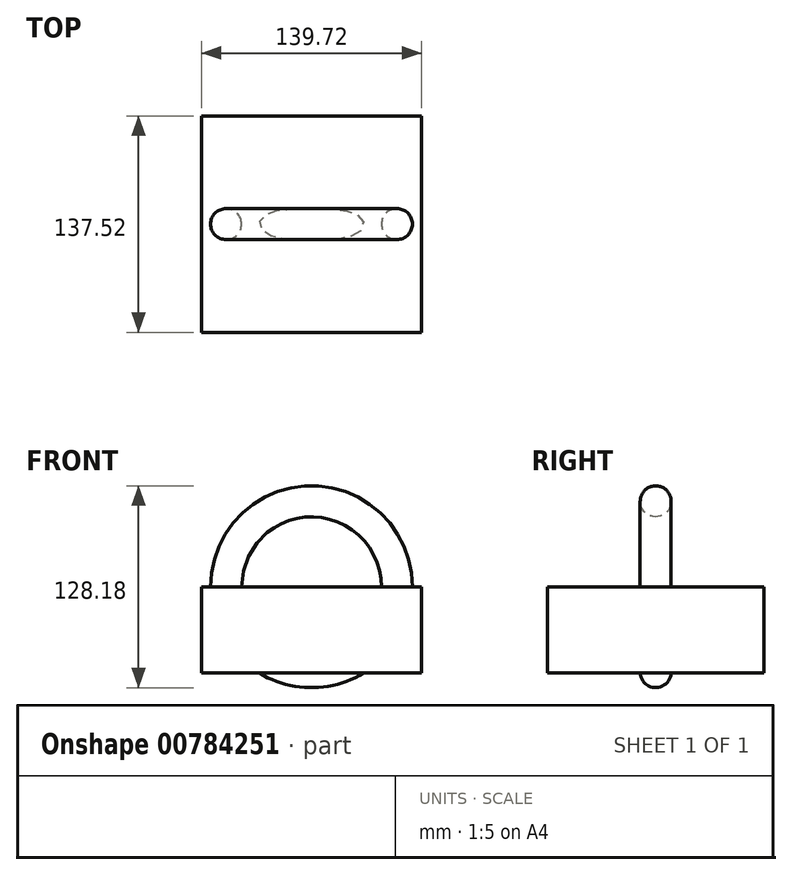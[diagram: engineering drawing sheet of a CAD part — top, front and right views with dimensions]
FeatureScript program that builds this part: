
annotation { "Feature Type Name" : "Feature", "Feature Type Description" : "" }
export const myFeature = defineFeature(function(context is Context, id is Id, definition is map)
    precondition{}
    {
        {
            var Q0;
            Q0=qCreatedBy(makeId("Top.planeOp"),FACE);
            var sketch = newSketch(context, id + "F0", { "sketchPlane" : qUnion([Q0])});
            skLineSegment(sketch, "E0.bottom", {"start": v(69.86, -68.76) * mm, "end": v(-69.86, -68.76) * mm});
            skLineSegment(sketch, "E0.top", {"start": v(69.86, 68.76) * mm, "end": v(-69.86, 68.76) * mm});
            skLineSegment(sketch, "E0.left", {"start": v(69.86, -68.76) * mm, "end": v(69.86, 68.76) * mm});
            skLineSegment(sketch, "E0.right", {"start": v(-69.86, -68.76) * mm, "end": v(-69.86, 68.76) * mm});
            skPoint(sketch, "E0.middle", {"position": v(0, 0) * mm});
            skLineSegment(sketch, "E1", {"start": v(0, 68.76) * mm, "end": v(0, -68.76) * mm});
            skSolve(sketch);
        }
        {
            var Q0;
            Q0=qCreatedBy(makeId("Top.planeOp"),FACE);
            var sketch = newSketch(context, id + "F1", { "sketchPlane" : qUnion([Q0])});
            skCircle(sketch, "E2", {"center": v(54.26, 0) * mm, "radius": 9.82 * mm});
            skSolve(sketch);
        }
        {
            var Q0;
            {var subQ0=sQuery(id+"F0.wireOp",EDGE,"E0.right");Q0=makeQuery(id+"F0.imprint","IMPRINT",FACE,{"disambiguationData":[TD([[makeQuery(id+"F0.imprint","IMPRINT",EDGE,{"derivedFrom":subQ0}),-1.0]])]});}
            var Q1;
            {var subQ0=sQuery(id+"F0.wireOp",EDGE,"E0.left");Q1=makeQuery(id+"F0.imprint","IMPRINT",FACE,{"disambiguationData":[TD([[makeQuery(id+"F0.imprint","IMPRINT",EDGE,{"derivedFrom":subQ0}),1.0]])]});}
            extrude(context, id + "F2", {"entities" : qUnion([Q0, Q1]), "oppositeDirection" : true, "depth" : 54.86 * mm, "offsetDistance" : 25.4 * mm});
        }
        {
            var Q0;
            Q0=makeQuery(id+"F1.imprint","IMPRINT",FACE,{"disambiguationData":[TD([[makeQuery(id+"F1.imprint","IMPRINT",EDGE,{"derivedFrom":sQuery(id+"F1.wireOp",EDGE,"E2")}),1.0]])]});
            var Q1;
            Q1=sQuery(id+"F0.wireOp",EDGE,"E1");
            revolve(context, id + "F3", {"operationType" : NewBodyOperationType.ADD, "surfaceOperationType" : NewSurfaceOperationType.NEW, "entities" : qUnion([Q0]), "axis" : qUnion([Q1]), "revolveType" : RevolveType.FULL});
        }
    });
